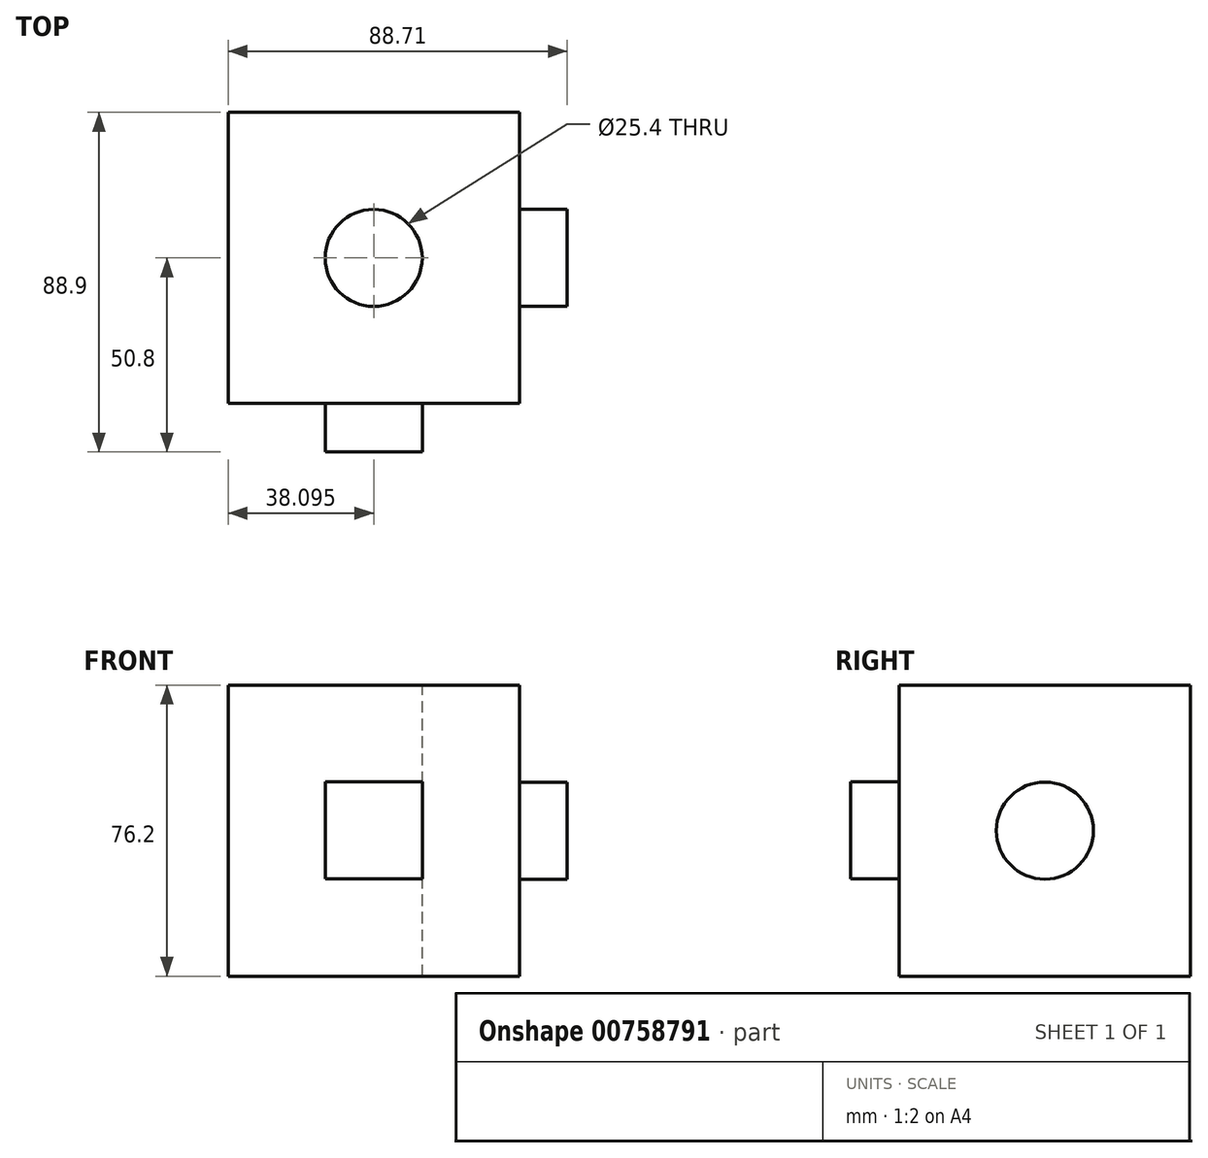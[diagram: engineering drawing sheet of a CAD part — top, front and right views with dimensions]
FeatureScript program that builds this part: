
annotation { "Feature Type Name" : "Feature", "Feature Type Description" : "" }
export const myFeature = defineFeature(function(context is Context, id is Id, definition is map)
    precondition{}
    {
        {
            var Q0;
            Q0=qCreatedBy(makeId("Front.planeOp"),FACE);
            var sketch = newSketch(context, id + "F0", { "sketchPlane" : qUnion([Q0])});
            skLineSegment(sketch, "E0.bottom", {"start": v(-30.3, 50.76) * mm, "end": v(45.9, 50.76) * mm});
            skLineSegment(sketch, "E0.top", {"start": v(-30.3, -25.44) * mm, "end": v(45.9, -25.44) * mm});
            skLineSegment(sketch, "E0.left", {"start": v(-30.3, 50.76) * mm, "end": v(-30.3, -25.44) * mm});
            skLineSegment(sketch, "E0.right", {"start": v(45.9, 50.76) * mm, "end": v(45.9, -25.44) * mm});
            skSolve(sketch);
        }
        {
            var Q0;
            Q0=makeQuery(id+"F0.imprint","IMPRINT",FACE,{"disambiguationData":[TD([[makeQuery(id+"F0.imprint","IMPRINT",EDGE,{"derivedFrom":sQuery(id+"F0.wireOp",EDGE,"E0.bottom")}),-1.0]])]});
            extrude(context, id + "F1", {"entities" : qUnion([Q0]), "depth" : 76.2 * mm, "offsetDistance" : 25.4 * mm});
        }
        {
            var Q0;
            Q0=qCreatedBy(makeId("Right.planeOp"),FACE);
            var sketch = newSketch(context, id + "F2", { "sketchPlane" : qUnion([Q0])});
            skCircle(sketch, "E1", {"center": v(-38.1, 12.66) * mm, "radius": 12.7 * mm});
            skSolve(sketch);
        }
        {
            var Q0;
            Q0 = qSketchRegion(id + "F2", true);
            extrude(context, id + "F3", {"entities" : qUnion([Q0]), "operationType" : NewBodyOperationType.ADD, "depth" : 58.42 * mm, "offsetDistance" : 25.4 * mm});
        }
        {
            var Q0;
            Q0=makeQuery(id+"F1.opExtrude","SWEPT_FACE",FACE,{"disambiguationData":[OSD([sQuery(id+"F0.wireOp",EDGE,"E0.bottom")])]});
            var sketch = newSketch(context, id + "F4", { "sketchPlane" : qUnion([Q0])});
            skPoint(sketch, "E2", {"position": v(7.8, -38.1) * mm});
            skSolve(sketch);
        }
        {
            var Q0;
            Q0=sQuery(id+"F4.wireOp",VERTEX,"E2");
            var Q1;
            Q1=makeQuery(id+"F1.opExtrude","SWEPT_BODY",BODY,{"disambiguationData":[OSD([sQuery(id+"F0.wireOp",EDGE,"E0.bottom"),sQuery(id+"F0.wireOp",EDGE,"E0.top"),sQuery(id+"F0.wireOp",EDGE,"E0.left"),sQuery(id+"F0.wireOp",EDGE,"E0.right")])]});
            hole(context, id + "F5", {"style" : HoleStyle.SIMPLE, "endStyle" : HoleEndStyle.THROUGH, "holeDiameter" : 25.4 * mm, "majorDiameter" : 6.35 * mm, "isTappedThrough" : true, "tappedDepth" : 12.7 * mm, "tapClearance" : 3, "locations" : qUnion([Q0]), "scope" : qUnion([Q1])});
        }
        {
            var Q0;
            Q0=makeQuery(id+"F1.opExtrude","CAP_FACE",FACE,{"disambiguationData":[OSD([sQuery(id+"F0.wireOp",EDGE,"E0.bottom"),sQuery(id+"F0.wireOp",EDGE,"E0.top"),sQuery(id+"F0.wireOp",EDGE,"E0.left"),sQuery(id+"F0.wireOp",EDGE,"E0.right")])],"isStart":false});
            var sketch = newSketch(context, id + "F6", { "sketchPlane" : qUnion([Q0])});
            skLineSegment(sketch, "E3.bottom", {"start": v(-4.9, 25.4) * mm, "end": v(20.5, 25.4) * mm});
            skLineSegment(sketch, "E3.top", {"start": v(-4.9, 0) * mm, "end": v(20.5, 0) * mm});
            skLineSegment(sketch, "E3.left", {"start": v(-4.9, 25.4) * mm, "end": v(-4.9, 0) * mm});
            skLineSegment(sketch, "E3.right", {"start": v(20.5, 25.4) * mm, "end": v(20.5, 0) * mm});
            skSolve(sketch);
        }
        {
            var Q0;
            Q0 = qSketchRegion(id + "F6", true);
            var Q1;
            Q1=makeQuery(id+"F6.imprint","IMPRINT",FACE,{"disambiguationData":[TD([[makeQuery(id+"F6.imprint","IMPRINT",EDGE,{"derivedFrom":sQuery(id+"F6.wireOp",EDGE,"E3.bottom")}),-1.0]])]});
            extrude(context, id + "F7", {"entities" : qUnion([Q0, Q1]), "operationType" : NewBodyOperationType.ADD, "depth" : 12.7 * mm, "offsetDistance" : 25.4 * mm});
        }
    });
